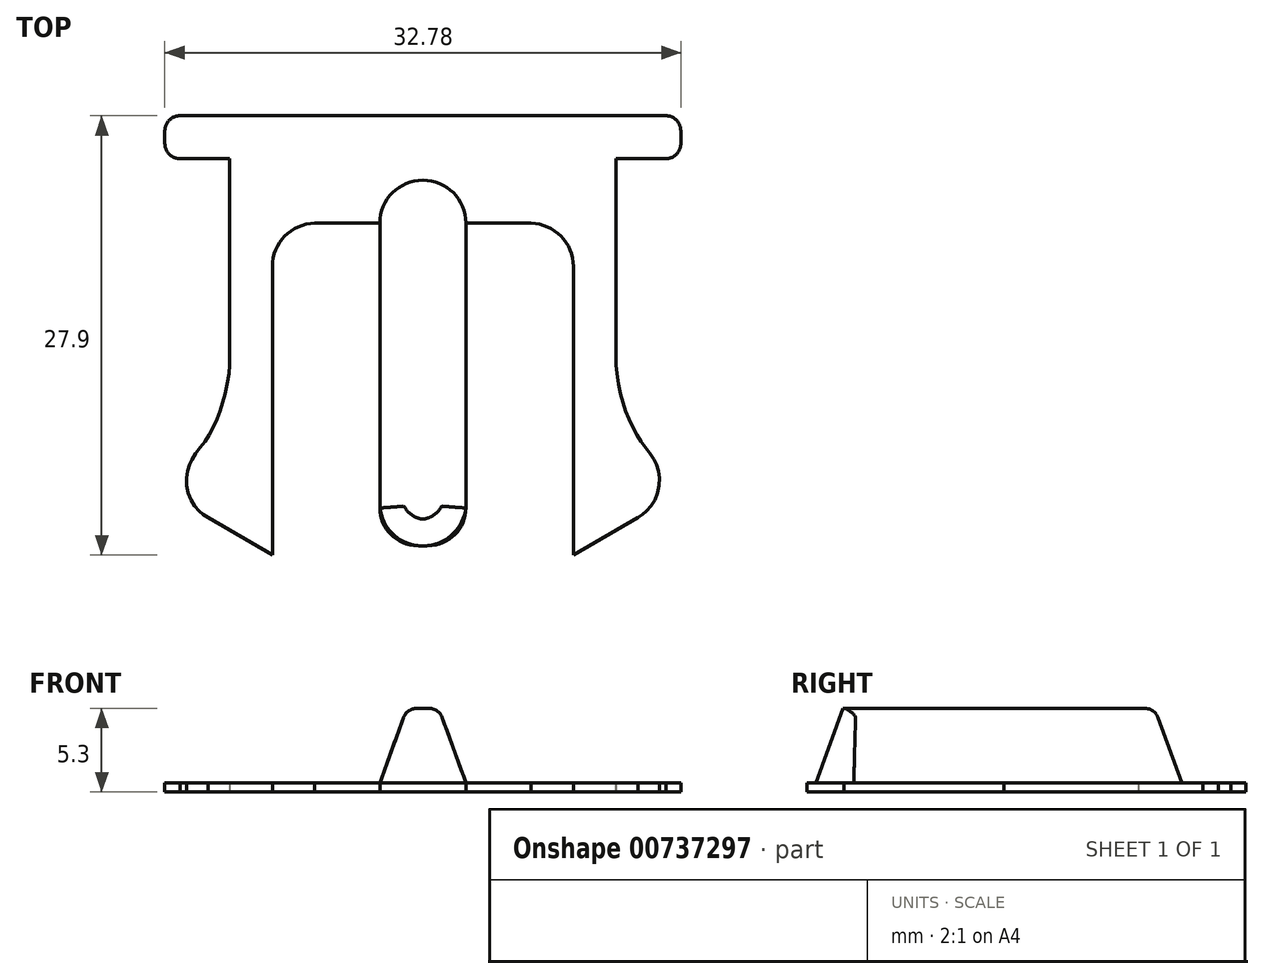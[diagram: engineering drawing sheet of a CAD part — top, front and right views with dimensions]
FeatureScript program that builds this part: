
annotation { "Feature Type Name" : "Feature", "Feature Type Description" : "" }
export const myFeature = defineFeature(function(context is Context, id is Id, definition is map)
    precondition{}
    {
        {
            var Q0;
            Q0=qCreatedBy(makeId("Top.planeOp"),FACE);
            var sketch = newSketch(context, id + "F0", { "sketchPlane" : qUnion([Q0])});
            skLineSegment(sketch, "E0", {"start": v(-10.4, 7.18) * mm, "end": v(-13.08, 7.18) * mm});
            skFitSpline(sketch, "E1", {"points": [v(-13.08, 7.18) * mm, v(-13.21, 7.2) * mm, v(-13.31, 7.22) * mm, v(-13.44, 7.27) * mm, v(-13.65, 7.42) * mm, v(-13.73, 7.54) * mm, v(-13.8, 7.66) * mm, v(-13.86, 7.8) * mm, v(-13.89, 8) * mm], "startDerivative": vector(-1.38, 0.14) * mm, "endDerivative": vector(-0.27, 1.3) * mm});
            skLineSegment(sketch, "E2", {"start": v(0, -2.32) * mm, "end": v(0, 17.74) * mm, "construction": true});
            skLineSegment(sketch, "E3", {"start": v(-13.89, 8) * mm, "end": v(-13.89, 8.69) * mm});
            skFitSpline(sketch, "E4", {"points": [v(-13.89, 8.69) * mm, v(-13.87, 8.8) * mm, v(-13.86, 8.87) * mm, v(-13.84, 8.96) * mm, v(-13.8, 9.04) * mm, v(-13.74, 9.14) * mm, v(-13.68, 9.22) * mm, v(-13.6, 9.3) * mm, v(-13.52, 9.36) * mm, v(-13.43, 9.41) * mm, v(-13.35, 9.45) * mm, v(-13.27, 9.47) * mm, v(-13.2, 9.49) * mm, v(-13.08, 9.5) * mm], "startDerivative": vector(0.22, 1.27) * mm, "endDerivative": vector(1.16, 0.03) * mm});
            skLineSegment(sketch, "E5", {"start": v(-13.08, 9.5) * mm, "end": v(0, 9.5) * mm});
            skLineSegment(sketch, "E6", {"start": v(-10.4, 7.18) * mm, "end": v(-10.4, -3.54) * mm});
            skFitSpline(sketch, "E7", {"points": [v(-10.4, -3.54) * mm, v(-10.4, -4.06) * mm, v(-10.56, -5.11) * mm, v(-10.79, -6) * mm, v(-11.04, -6.72) * mm, v(-11.42, -7.52) * mm, v(-11.74, -8.04) * mm, v(-12.1, -8.53) * mm, v(-12.41, -8.96) * mm, v(-12.57, -9.28) * mm, v(-12.7, -9.74) * mm, v(-12.72, -10.27) * mm, v(-12.61, -10.88) * mm, v(-12.38, -11.35) * mm, v(-12.09, -11.73) * mm, v(-11.83, -11.96) * mm, v(-11.57, -12.14) * mm], "startDerivative": vector(0.58, -8.43) * mm, "endDerivative": vector(8.37, -6.5) * mm});
            skLineSegment(sketch, "E8", {"start": v(-11.57, -12.14) * mm, "end": v(-8.1, -14.14) * mm});
            skLineSegment(sketch, "E9", {"start": v(-8.1, -14.14) * mm, "end": v(-8.1, 1.38) * mm});
            skArc(sketch, "E10", {"start": v(-5.82, 3.7) * mm, "mid": v(-7.43, 3.01) * mm, "end": v(-8.1, 1.38) * mm});
            skLineSegment(sketch, "E11", {"start": v(-5.82, 3.7) * mm, "end": v(-2.32, 3.71) * mm});
            skLineSegment(sketch, "E12", {"start": v(-2.32, 3.71) * mm, "end": v(-2.32, -11.62) * mm});
            skArc(sketch, "E13", {"start": v(-2.32, -11.62) * mm, "mid": v(-1.72, -13.05) * mm, "end": v(-0.3, -13.64) * mm});
            skLineSegment(sketch, "E14", {"start": v(-0.3, -13.64) * mm, "end": v(0, -13.65) * mm});
            skLineSegment(sketch, "E15.MirrorCS", {"start": v(13.89, 8) * mm, "end": v(13.89, 8.69) * mm});
            skFitSpline(sketch, "E16.MirrorCS", {"points": [v(13.89, 8.69) * mm, v(13.87, 8.8) * mm, v(13.86, 8.87) * mm, v(13.84, 8.96) * mm, v(13.8, 9.04) * mm, v(13.74, 9.14) * mm, v(13.68, 9.22) * mm, v(13.6, 9.3) * mm, v(13.52, 9.36) * mm, v(13.43, 9.41) * mm, v(13.35, 9.45) * mm, v(13.27, 9.47) * mm, v(13.2, 9.49) * mm, v(13.08, 9.5) * mm], "startDerivative": vector(-0.22, 1.27) * mm, "endDerivative": vector(-1.16, 0.03) * mm});
            skFitSpline(sketch, "E17.MirrorCS", {"points": [v(13.08, 7.18) * mm, v(13.21, 7.2) * mm, v(13.31, 7.22) * mm, v(13.44, 7.27) * mm, v(13.65, 7.42) * mm, v(13.73, 7.54) * mm, v(13.8, 7.66) * mm, v(13.86, 7.8) * mm, v(13.89, 8) * mm], "startDerivative": vector(1.38, 0.14) * mm, "endDerivative": vector(0.27, 1.3) * mm});
            skLineSegment(sketch, "E18.MirrorCS", {"start": v(0.3, -13.64) * mm, "end": v(0, -13.65) * mm});
            skFitSpline(sketch, "E19.MirrorCS", {"points": [v(10.4, -3.54) * mm, v(10.4, -4.06) * mm, v(10.56, -5.11) * mm, v(10.79, -6) * mm, v(11.04, -6.72) * mm, v(11.42, -7.52) * mm, v(11.74, -8.04) * mm, v(12.1, -8.53) * mm, v(12.41, -8.96) * mm, v(12.57, -9.28) * mm, v(12.7, -9.74) * mm, v(12.72, -10.27) * mm, v(12.61, -10.88) * mm, v(12.38, -11.35) * mm, v(12.09, -11.73) * mm, v(11.83, -11.96) * mm, v(11.57, -12.14) * mm], "startDerivative": vector(-0.58, -8.43) * mm, "endDerivative": vector(-8.37, -6.5) * mm});
            skArc(sketch, "E20.MirrorCS", {"start": v(2.32, -11.62) * mm, "mid": v(1.72, -13.05) * mm, "end": v(0.3, -13.64) * mm});
            skLineSegment(sketch, "E21.MirrorCS", {"start": v(10.4, 7.18) * mm, "end": v(13.08, 7.18) * mm});
            skLineSegment(sketch, "E22.MirrorCS", {"start": v(2.32, 3.71) * mm, "end": v(2.32, -11.62) * mm});
            skLineSegment(sketch, "E23.MirrorCS", {"start": v(5.82, 3.7) * mm, "end": v(2.32, 3.71) * mm});
            skArc(sketch, "E24.MirrorCS", {"start": v(5.82, 3.7) * mm, "mid": v(7.43, 3.01) * mm, "end": v(8.1, 1.38) * mm});
            skLineSegment(sketch, "E25.MirrorCS", {"start": v(8.1, -14.14) * mm, "end": v(8.1, 1.38) * mm});
            skLineSegment(sketch, "E26.MirrorCS", {"start": v(11.57, -12.14) * mm, "end": v(8.1, -14.14) * mm});
            skLineSegment(sketch, "E27.MirrorCS", {"start": v(13.08, 9.5) * mm, "end": v(0, 9.5) * mm});
            skLineSegment(sketch, "E28.MirrorCS", {"start": v(10.4, 7.18) * mm, "end": v(10.4, -3.54) * mm});
            skSolve(sketch);
        }
        {
            var Q0;
            Q0 = qSketchRegion(id + "F0", true);
            extrude(context, id + "F1", {"entities" : qUnion([Q0]), "depth" : 0.49 * mm, "offsetDistance" : 25 * mm});
        }
        {
            var Q0;
            Q0=makeQuery(id+"F1.opExtrude","SWEPT_FACE",FACE,{"disambiguationData":[OSD([sQuery(id+"F0.wireOp",EDGE,"E11")])]});
            cPlane(context, id + "F2", {"entities" : qUnion([Q0]), "cplaneType" : CPlaneType.OFFSET, "offset" : 0 * mm, "width" : 150 * mm, "height" : 150 * mm});
        }
        {
            var Q0;
            Q0=makeQuery(id+"F1.opExtrude","CAP_FACE",FACE,{"disambiguationData":[OSD([sQuery(id+"F0.wireOp",EDGE,"E0"),sQuery(id+"F0.wireOp",EDGE,"E1"),sQuery(id+"F0.wireOp",EDGE,"E3"),sQuery(id+"F0.wireOp",EDGE,"E4"),sQuery(id+"F0.wireOp",EDGE,"E5"),sQuery(id+"F0.wireOp",EDGE,"E6"),sQuery(id+"F0.wireOp",EDGE,"E7"),sQuery(id+"F0.wireOp",EDGE,"E8"),sQuery(id+"F0.wireOp",EDGE,"E9"),sQuery(id+"F0.wireOp",EDGE,"E10"),sQuery(id+"F0.wireOp",EDGE,"E11"),sQuery(id+"F0.wireOp",EDGE,"E12"),sQuery(id+"F0.wireOp",EDGE,"E13"),sQuery(id+"F0.wireOp",EDGE,"E14"),sQuery(id+"F0.wireOp",EDGE,"E15.MirrorCS"),sQuery(id+"F0.wireOp",EDGE,"E16.MirrorCS"),sQuery(id+"F0.wireOp",EDGE,"E17.MirrorCS"),sQuery(id+"F0.wireOp",EDGE,"E18.MirrorCS"),sQuery(id+"F0.wireOp",EDGE,"E19.MirrorCS"),sQuery(id+"F0.wireOp",EDGE,"E20.MirrorCS"),sQuery(id+"F0.wireOp",EDGE,"E21.MirrorCS"),sQuery(id+"F0.wireOp",EDGE,"E22.MirrorCS"),sQuery(id+"F0.wireOp",EDGE,"E23.MirrorCS"),sQuery(id+"F0.wireOp",EDGE,"E24.MirrorCS"),sQuery(id+"F0.wireOp",EDGE,"E25.MirrorCS"),sQuery(id+"F0.wireOp",EDGE,"E26.MirrorCS"),sQuery(id+"F0.wireOp",EDGE,"E27.MirrorCS"),sQuery(id+"F0.wireOp",EDGE,"E28.MirrorCS")])],"isStart":false});
            var sketch = newSketch(context, id + "F3", { "sketchPlane" : qUnion([Q0])});
            skLineSegment(sketch, "E29", {"start": v(-2.32, 3.71) * mm, "end": v(-2.32, -11.62) * mm});
            skArc(sketch, "E30", {"start": v(-2.32, -11.62) * mm, "mid": v(0, -13.66) * mm, "end": v(2.32, -11.62) * mm});
            skLineSegment(sketch, "E31", {"start": v(2.32, -11.62) * mm, "end": v(2.32, 3.71) * mm});
            skArc(sketch, "E32", {"start": v(2.32, 3.71) * mm, "mid": v(0, 6.03) * mm, "end": v(-2.32, 3.71) * mm});
            skSolve(sketch);
        }
        {
            var Q0;
            Q0 = qSketchRegion(id + "F3", true);
            extrude(context, id + "F4", {"entities" : qUnion([Q0]), "operationType" : NewBodyOperationType.ADD, "depth" : 4 * mm, "offsetDistance" : 25 * mm, "hasDraft" : true, "draftAngle" : 20 * degree, "draftPullDirection" : true});
        }
        {
            var Q0;
            Q0=makeQuery(id+"F4.opExtrude","CAP_EDGE",EDGE,{"disambiguationData":[OSD([sQuery(id+"F3.wireOp",EDGE,"E31")])],"isStart":false});
            fillet(context, id + "F5", {"entities" : qUnion([Q0]), "radius" : 0.75 * mm, "tangentPropagation" : true, "allowEdgeOverflow" : false});
        }
        {
            var Q0;
            Q0=makeQuery(id+"F1.opExtrude","SWEPT_BODY",BODY,{"disambiguationData":[OSD([sQuery(id+"F0.wireOp",EDGE,"E0"),sQuery(id+"F0.wireOp",EDGE,"E1"),sQuery(id+"F0.wireOp",EDGE,"E3"),sQuery(id+"F0.wireOp",EDGE,"E4"),sQuery(id+"F0.wireOp",EDGE,"E5"),sQuery(id+"F0.wireOp",EDGE,"E6"),sQuery(id+"F0.wireOp",EDGE,"E7"),sQuery(id+"F0.wireOp",EDGE,"E8"),sQuery(id+"F0.wireOp",EDGE,"E9"),sQuery(id+"F0.wireOp",EDGE,"E10"),sQuery(id+"F0.wireOp",EDGE,"E11"),sQuery(id+"F0.wireOp",EDGE,"E12"),sQuery(id+"F0.wireOp",EDGE,"E13"),sQuery(id+"F0.wireOp",EDGE,"E14"),sQuery(id+"F0.wireOp",EDGE,"E15.MirrorCS"),sQuery(id+"F0.wireOp",EDGE,"E16.MirrorCS"),sQuery(id+"F0.wireOp",EDGE,"E17.MirrorCS"),sQuery(id+"F0.wireOp",EDGE,"E18.MirrorCS"),sQuery(id+"F0.wireOp",EDGE,"E19.MirrorCS"),sQuery(id+"F0.wireOp",EDGE,"E20.MirrorCS"),sQuery(id+"F0.wireOp",EDGE,"E21.MirrorCS"),sQuery(id+"F0.wireOp",EDGE,"E22.MirrorCS"),sQuery(id+"F0.wireOp",EDGE,"E23.MirrorCS"),sQuery(id+"F0.wireOp",EDGE,"E24.MirrorCS"),sQuery(id+"F0.wireOp",EDGE,"E25.MirrorCS"),sQuery(id+"F0.wireOp",EDGE,"E26.MirrorCS"),sQuery(id+"F0.wireOp",EDGE,"E27.MirrorCS"),sQuery(id+"F0.wireOp",EDGE,"E28.MirrorCS")])]});
            var Q1;
            Q1=qCreatedBy(makeId("Origin.pointOp"),VERTEX);
            transform(context, id + "F6", {"entities" : qUnion([Q0]), "transformType" : TransformType.SCALE_UNIFORMLY, "scale" : 1.18, "scalePoint" : qUnion([Q1]), "makeCopy" : false});
        }
    });
